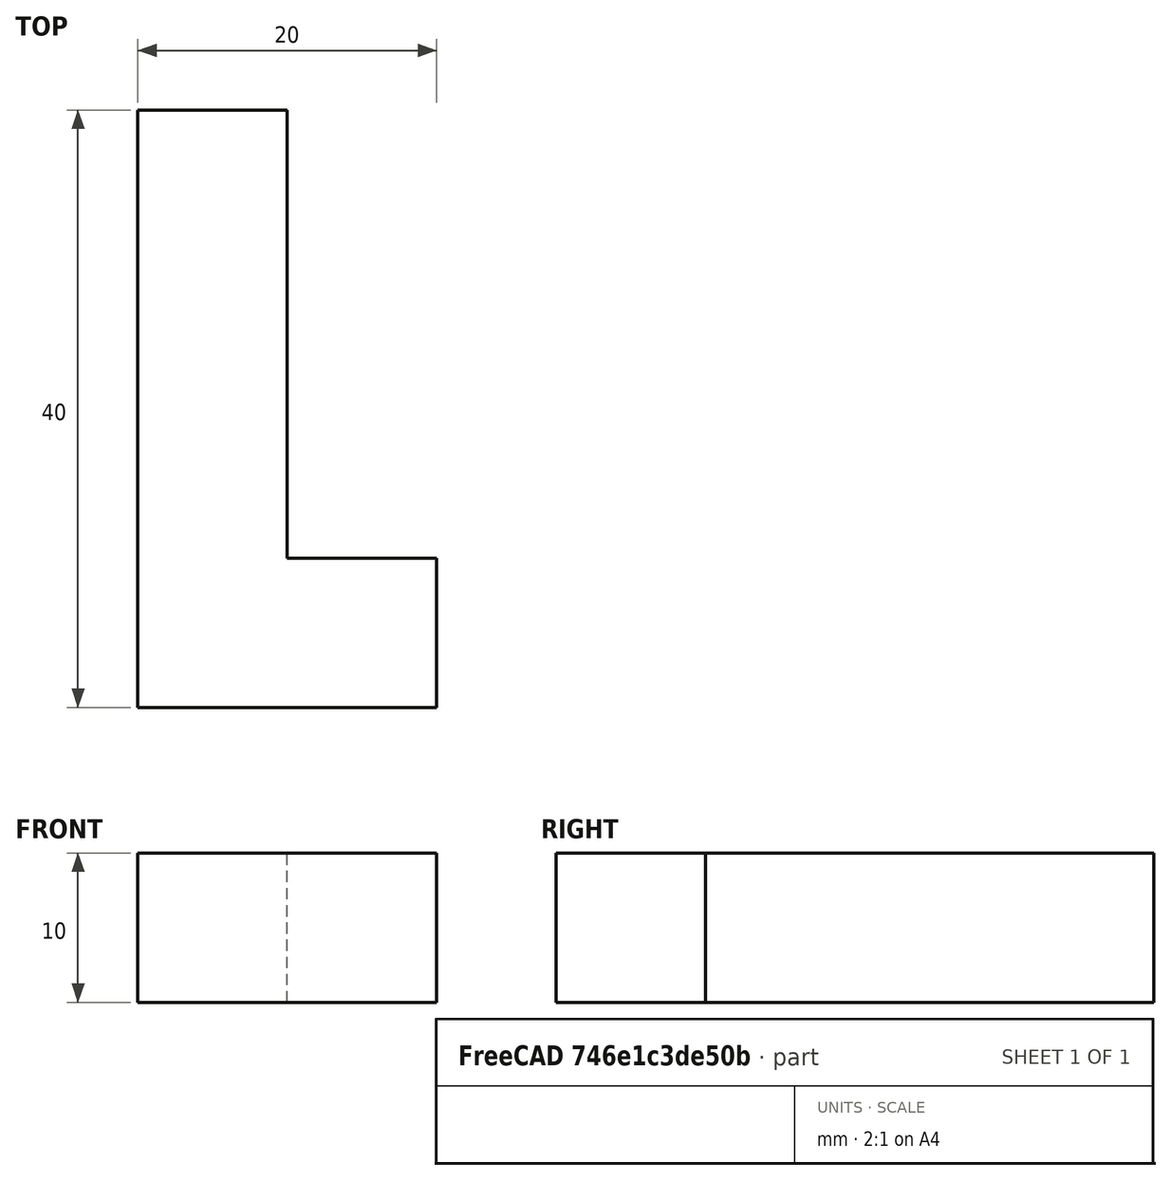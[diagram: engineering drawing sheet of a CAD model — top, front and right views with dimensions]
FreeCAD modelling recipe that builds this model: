
FCSTD DOCUMENT  (FreeCAD 0.16R)
Label: L
License: All rights reserved
LicenseURL: http://en.wikipedia.org/wiki/All_rights_reserved
objects: Sketcher::SketchObject×1, PartDesign::Pad×1, Mesh::Feature×1
note: 3 computed .brp shape members not serialized (recipe doc carries the construction recipe); baked Part::Feature solids carry a one-line shape summary decoded from their .brp

FEATURE [Sketcher::SketchObject] Sketch
  sketch-geometry (6):
    g0: LineSegment StartX=-20 StartY=40 StartZ=0 EndX=-20 EndY=0 EndZ=0
    g1: LineSegment StartX=-20 StartY=0 StartZ=0 EndX=0 EndY=0 EndZ=0
    g2: LineSegment StartX=0 StartY=0 StartZ=0 EndX=4.93577e-07 EndY=10 EndZ=0
    g3: LineSegment StartX=4.93577e-07 StartY=10 StartZ=0 EndX=-10 EndY=10 EndZ=0
    g4: LineSegment StartX=-10 StartY=10 StartZ=0 EndX=-10 EndY=40 EndZ=0
    g5: LineSegment StartX=-10 StartY=40 StartZ=0 EndX=-20 EndY=40 EndZ=0
  constraints (17):
    c: Coincident(g0,g1)
    c: Horizontal(g1)
    c: Coincident(g1,g2)
    c: Coincident(g2,g3)
    c: Horizontal(g3)
    c: Coincident(g3,g4)
    c: Coincident(g4,g5)
    c: Coincident(g5,g0)
    c: Horizontal(g5)
    c: Distance(g0) = 40
    c: Distance(g2) = 10
    c: Distance(g3) = 10
    c: Distance(g4) = 30
    c: Distance(g5) = 10
    c: Perpendicular(g0,g1)
    c: Coincident(g1,g-1)
    c: Distance(g1) = 20
FEATURE [PartDesign::Pad] Pad
  Length = 10
  Length2 = 100
  Sketch = -> Sketch
  Type = 0
FEATURE [Mesh::Feature] Mesh  label="Pad (Meshed)"
